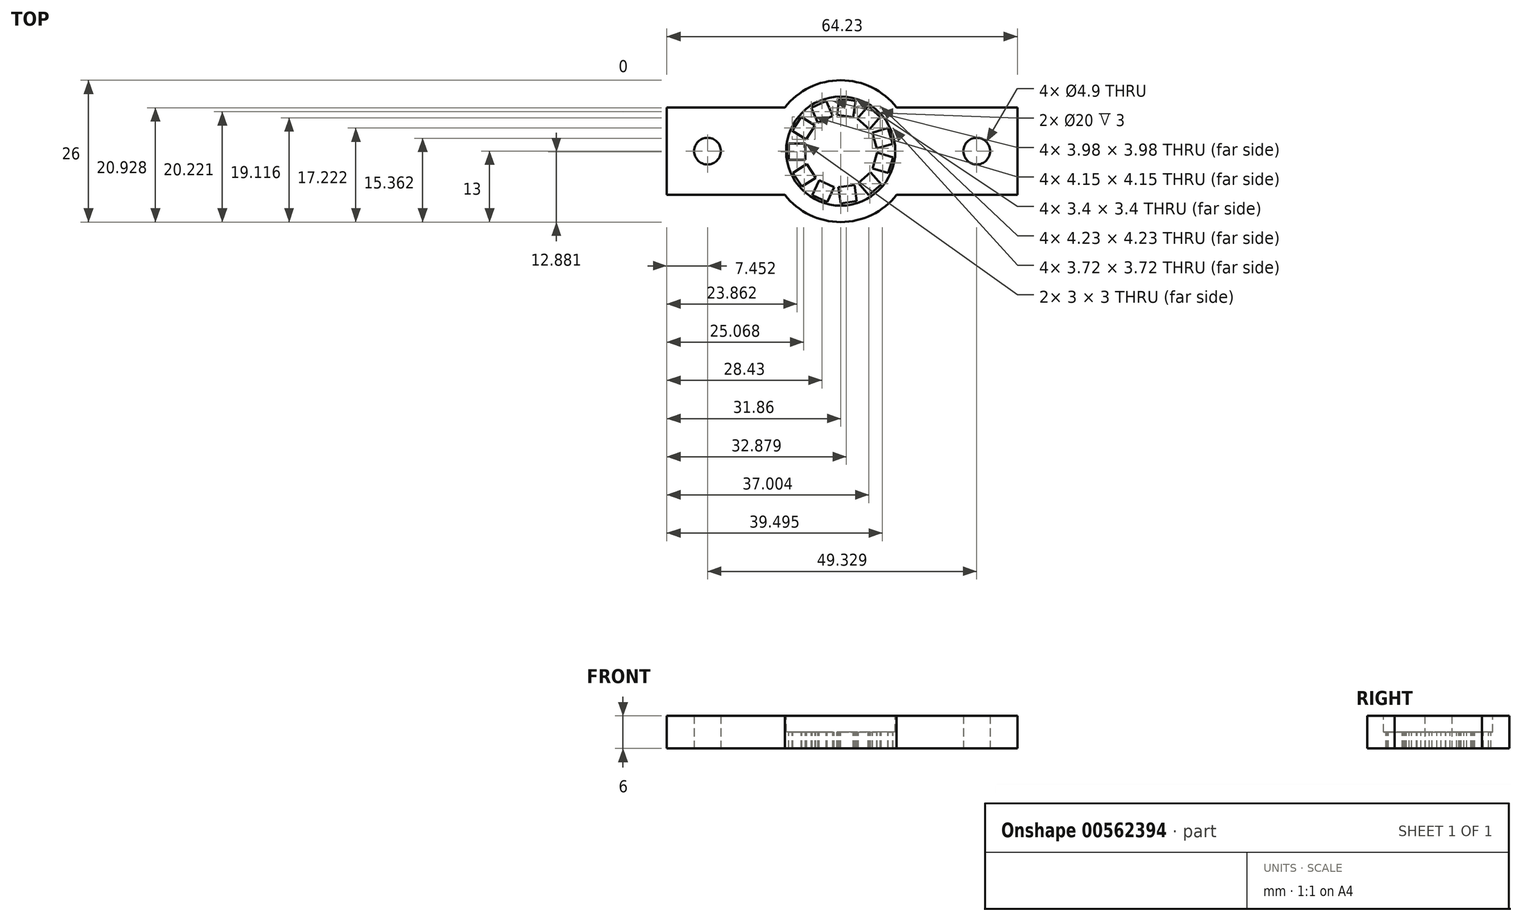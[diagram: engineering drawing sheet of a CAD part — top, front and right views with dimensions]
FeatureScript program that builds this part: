
annotation { "Feature Type Name" : "Feature", "Feature Type Description" : "" }
export const myFeature = defineFeature(function(context is Context, id is Id, definition is map)
    precondition{}
    {
        {
            var Q0;
            Q0=qCreatedBy(makeId("Top.planeOp"),FACE);
            var sketch = newSketch(context, id + "F0", { "sketchPlane" : qUnion([Q0])});
            skCircle(sketch, "E0", {"center": v(0, 0) * mm, "radius": 13 * mm});
            skLineSegment(sketch, "E1", {"start": v(10.25, 8) * mm, "end": v(32.37, 8) * mm});
            skLineSegment(sketch, "E2", {"start": v(32.37, 8) * mm, "end": v(32.37, -8) * mm});
            skLineSegment(sketch, "E3", {"start": v(32.37, -8) * mm, "end": v(10.25, -8) * mm});
            skCircle(sketch, "E4", {"center": v(24.92, 0) * mm, "radius": 2.45 * mm});
            skLineSegment(sketch, "E5", {"start": v(-10.25, -8) * mm, "end": v(-31.86, -8) * mm});
            skLineSegment(sketch, "E6", {"start": v(-31.86, -8) * mm, "end": v(-31.86, 8) * mm});
            skLineSegment(sketch, "E7", {"start": v(-31.86, 8) * mm, "end": v(-10.25, 8) * mm});
            skCircle(sketch, "E8", {"center": v(-24.4, 0) * mm, "radius": 2.45 * mm});
            skSolve(sketch);
        }
        {
            var Q0;
            Q0=qSketchRegion(id+"F0",true);
            extrude(context, id + "F1", {"entities" : qUnion([Q0]), "depth" : 6 * mm, "offsetDistance" : 25 * mm});
        }
        {
            var Q0;
            Q0=makeQuery(id+"F1.opExtrude","CAP_FACE",FACE,{"disambiguationData":[OSD([sQuery(id+"F0.wireOp",EDGE,"E0"),sQuery(id+"F0.wireOp",EDGE,"E1"),sQuery(id+"F0.wireOp",EDGE,"E2"),sQuery(id+"F0.wireOp",EDGE,"E3"),sQuery(id+"F0.wireOp",EDGE,"E4"),sQuery(id+"F0.wireOp",EDGE,"E5"),sQuery(id+"F0.wireOp",EDGE,"E6"),sQuery(id+"F0.wireOp",EDGE,"E7"),sQuery(id+"F0.wireOp",EDGE,"E8")])],"isStart":false});
            var sketch = newSketch(context, id + "F2", { "sketchPlane" : qUnion([Q0])});
            skCircle(sketch, "E9", {"center": v(0, 0) * mm, "radius": 10 * mm});
            skSolve(sketch);
        }
        {
            var Q0;
            Q0=makeQuery(id+"F2.imprint","IMPRINT",FACE,{"disambiguationData":[TD([[makeQuery(id+"F2.imprint","IMPRINT",EDGE,{"derivedFrom":sQuery(id+"F2.wireOp",EDGE,"E9")}),1.0]])]});
            extrude(context, id + "F3", {"entities" : qUnion([Q0]), "operationType" : NewBodyOperationType.REMOVE, "oppositeDirection" : true, "depth" : 3 * mm, "offsetDistance" : 25 * mm});
        }
        {
            var Q0;
            Q0=makeQuery(id+"F3.boolean.opBoolean","COPY",FACE,{"derivedFrom":makeQuery(id+"F3.opExtrude","CAP_FACE",FACE,{"disambiguationData":[OSD([sQuery(id+"F2.wireOp",EDGE,"E9")])],"isStart":false})});
            var sketch = newSketch(context, id + "F4", { "sketchPlane" : qUnion([Q0])});
            skLineSegment(sketch, "E10.bottom", {"start": v(-9.5, 1.38) * mm, "end": v(-6.5, 1.38) * mm});
            skLineSegment(sketch, "E10.top", {"start": v(-9.5, -1.62) * mm, "end": v(-6.5, -1.62) * mm});
            skLineSegment(sketch, "E10.left", {"start": v(-9.5, 1.38) * mm, "end": v(-9.5, -1.62) * mm});
            skLineSegment(sketch, "E10.right", {"start": v(-6.5, 1.38) * mm, "end": v(-6.5, -1.62) * mm});
            skLineSegment(sketch, "E11.1.0", {"start": v(-6.22, -2.35) * mm, "end": v(-4.6, -4.87) * mm});
            skLineSegment(sketch, "E11.1.1", {"start": v(-8.74, -3.97) * mm, "end": v(-6.22, -2.35) * mm});
            skLineSegment(sketch, "E11.1.2", {"start": v(-8.74, -3.97) * mm, "end": v(-7.12, -6.5) * mm});
            skLineSegment(sketch, "E11.1.3", {"start": v(-7.12, -6.5) * mm, "end": v(-4.6, -4.87) * mm});
            skLineSegment(sketch, "E11.2.0", {"start": v(-3.96, -5.34) * mm, "end": v(-1.23, -6.58) * mm});
            skLineSegment(sketch, "E11.2.1", {"start": v(-5.2, -8.07) * mm, "end": v(-3.96, -5.34) * mm});
            skLineSegment(sketch, "E11.2.2", {"start": v(-5.2, -8.07) * mm, "end": v(-2.48, -9.31) * mm});
            skLineSegment(sketch, "E11.2.3", {"start": v(-2.48, -9.31) * mm, "end": v(-1.23, -6.58) * mm});
            skLineSegment(sketch, "E11.3.0", {"start": v(-0.45, -6.63) * mm, "end": v(2.52, -6.2) * mm});
            skLineSegment(sketch, "E11.3.1", {"start": v(-0.02, -9.6) * mm, "end": v(-0.45, -6.63) * mm});
            skLineSegment(sketch, "E11.3.2", {"start": v(-0.02, -9.6) * mm, "end": v(2.95, -9.17) * mm});
            skLineSegment(sketch, "E11.3.3", {"start": v(2.95, -9.17) * mm, "end": v(2.52, -6.2) * mm});
            skLineSegment(sketch, "E11.4.0", {"start": v(3.2, -5.82) * mm, "end": v(5.47, -3.85) * mm});
            skLineSegment(sketch, "E11.4.1", {"start": v(5.17, -8.08) * mm, "end": v(3.2, -5.82) * mm});
            skLineSegment(sketch, "E11.4.2", {"start": v(5.17, -8.08) * mm, "end": v(7.44, -6.12) * mm});
            skLineSegment(sketch, "E11.4.3", {"start": v(7.44, -6.12) * mm, "end": v(5.47, -3.85) * mm});
            skLineSegment(sketch, "E11.5.0", {"start": v(5.84, -3.16) * mm, "end": v(6.68, -0.28) * mm});
            skLineSegment(sketch, "E11.5.1", {"start": v(8.72, -4) * mm, "end": v(5.84, -3.16) * mm});
            skLineSegment(sketch, "E11.5.2", {"start": v(8.72, -4) * mm, "end": v(9.56, -1.13) * mm});
            skLineSegment(sketch, "E11.5.3", {"start": v(9.56, -1.13) * mm, "end": v(6.68, -0.28) * mm});
            skLineSegment(sketch, "E11.6.0", {"start": v(6.62, 0.5) * mm, "end": v(5.77, 3.38) * mm});
            skLineSegment(sketch, "E11.6.1", {"start": v(9.5, 1.34) * mm, "end": v(6.62, 0.5) * mm});
            skLineSegment(sketch, "E11.6.2", {"start": v(9.5, 1.34) * mm, "end": v(8.65, 4.22) * mm});
            skLineSegment(sketch, "E11.6.3", {"start": v(8.65, 4.22) * mm, "end": v(5.77, 3.38) * mm});
            skLineSegment(sketch, "E11.7.0", {"start": v(5.3, 4) * mm, "end": v(3.03, 5.96) * mm});
            skLineSegment(sketch, "E11.7.1", {"start": v(7.26, 6.27) * mm, "end": v(5.3, 4) * mm});
            skLineSegment(sketch, "E11.7.2", {"start": v(7.26, 6.27) * mm, "end": v(5, 8.23) * mm});
            skLineSegment(sketch, "E11.7.3", {"start": v(5, 8.23) * mm, "end": v(3.03, 5.96) * mm});
            skLineSegment(sketch, "E11.8.0", {"start": v(2.3, 6.23) * mm, "end": v(-0.68, 6.66) * mm});
            skLineSegment(sketch, "E11.8.1", {"start": v(2.72, 9.2) * mm, "end": v(2.3, 6.23) * mm});
            skLineSegment(sketch, "E11.8.2", {"start": v(2.72, 9.2) * mm, "end": v(-0.25, 9.63) * mm});
            skLineSegment(sketch, "E11.8.3", {"start": v(-0.25, 9.63) * mm, "end": v(-0.68, 6.66) * mm});
            skLineSegment(sketch, "E11.9.0", {"start": v(-1.44, 6.48) * mm, "end": v(-4.17, 5.23) * mm});
            skLineSegment(sketch, "E11.9.1", {"start": v(-2.69, 9.2) * mm, "end": v(-1.44, 6.48) * mm});
            skLineSegment(sketch, "E11.9.2", {"start": v(-2.69, 9.2) * mm, "end": v(-5.42, 7.96) * mm});
            skLineSegment(sketch, "E11.9.3", {"start": v(-5.42, 7.96) * mm, "end": v(-4.17, 5.23) * mm});
            skLineSegment(sketch, "E11.10.0", {"start": v(-4.72, 4.67) * mm, "end": v(-6.34, 2.15) * mm});
            skLineSegment(sketch, "E11.10.1", {"start": v(-7.24, 6.3) * mm, "end": v(-4.72, 4.67) * mm});
            skLineSegment(sketch, "E11.10.2", {"start": v(-7.24, 6.3) * mm, "end": v(-8.86, 3.77) * mm});
            skLineSegment(sketch, "E11.10.3", {"start": v(-8.86, 3.77) * mm, "end": v(-6.34, 2.15) * mm});
            skPoint(sketch, "E11.center", {"position": v(0, 0) * mm});
            skSolve(sketch);
        }
        {
            var Q0;
            Q0 = qSketchRegion(id + "F4", true);
            extrude(context, id + "F5", {"entities" : qUnion([Q0]), "operationType" : NewBodyOperationType.REMOVE, "endBound" : BoundingType.THROUGH_ALL, "oppositeDirection" : true, "depth" : 25 * mm, "offsetDistance" : 25 * mm});
        }
    });
